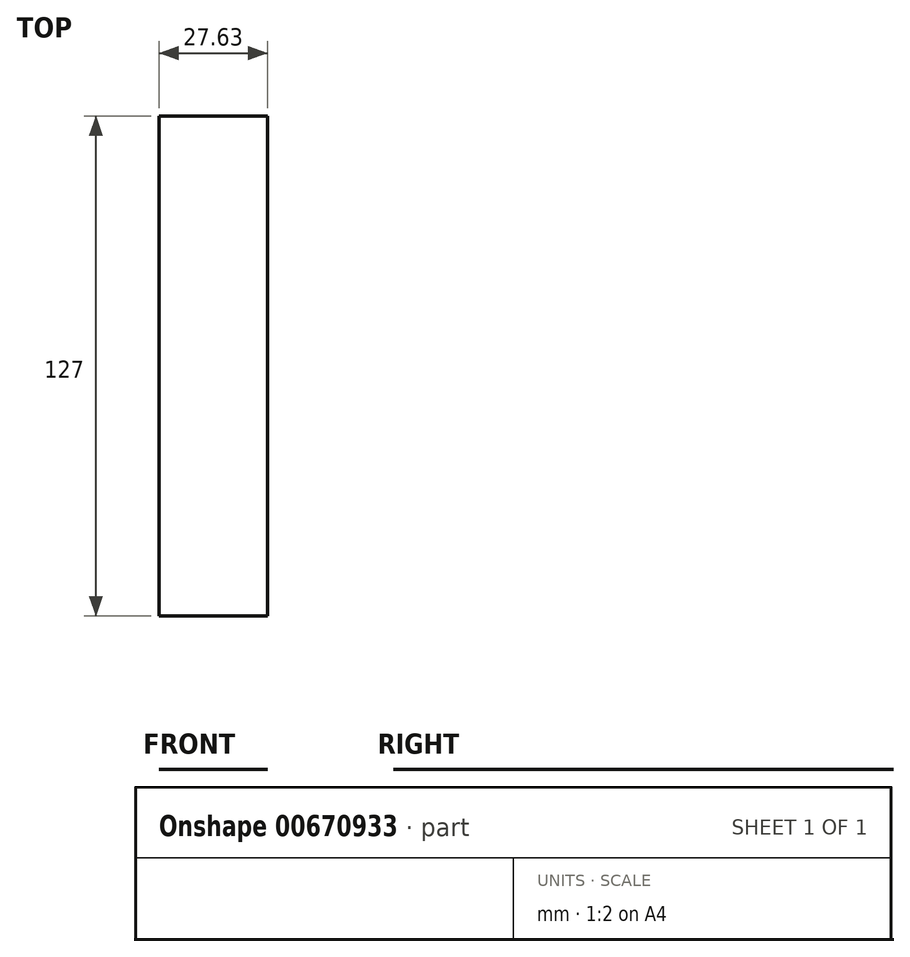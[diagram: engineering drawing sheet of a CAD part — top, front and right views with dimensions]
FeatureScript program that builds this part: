
annotation { "Feature Type Name" : "Feature", "Feature Type Description" : "" }
export const myFeature = defineFeature(function(context is Context, id is Id, definition is map)
    precondition{}
    {
        {
            var Q0;
            Q0=qCreatedBy(makeId("Front.planeOp"),FACE);
            var sketch = newSketch(context, id + "F0", { "sketchPlane" : qUnion([Q0])});
            skPoint(sketch, "E0.end.orphan", {"position": v(53.02, 30.37) * mm});
            skPoint(sketch, "E1.start.orphan", {"position": v(53.02, 15.58) * mm});
            skPoint(sketch, "E2.orphan", {"position": v(53.02, 28.12) * mm});
            skPoint(sketch, "E3.end.orphan", {"position": v(53.02, 3.05) * mm});
            skLineSegment(sketch, "E4", {"start": v(-59.12, 33.9) * mm, "end": v(-59.12, 5.94) * mm});
            skLineSegment(sketch, "E5", {"start": v(-59.12, 5.94) * mm, "end": v(-6.75, 5.94) * mm});
            skLineSegment(sketch, "E6", {"start": v(-6.75, 5.94) * mm, "end": v(-6.75, 33.9) * mm});
            skLineSegment(sketch, "E7", {"start": v(-59.12, 33.9) * mm, "end": v(-6.75, 33.9) * mm});
            skPoint(sketch, "E8.start.orphan", {"position": v(-57.52, -21.2) * mm});
            skPoint(sketch, "E9.start.orphan", {"position": v(-59.12, -14.3) * mm});
            skPoint(sketch, "E10.orphan", {"position": v(-55.91, -25.55) * mm});
            skPoint(sketch, "E11.start.orphan", {"position": v(-59.12, -16.87) * mm});
            skLineSegment(sketch, "E12", {"start": v(23.14, -22.33) * mm, "end": v(50.77, -22.33) * mm});
            skLineSegment(sketch, "E13", {"start": v(50.77, -24.9) * mm, "end": v(53.02, -29.72) * mm});
            skSolve(sketch);
        }
        {
            var Q0;
            Q0=sQuery(id+"F0.wireOp",EDGE,"E12");
            extrude(context, id + "F1", {"bodyType" : ToolBodyType.SURFACE, "surfaceEntities" : qUnion([Q0]), "depth" : 127 * mm, "offsetDistance" : 25.4 * mm});
        }
    });
